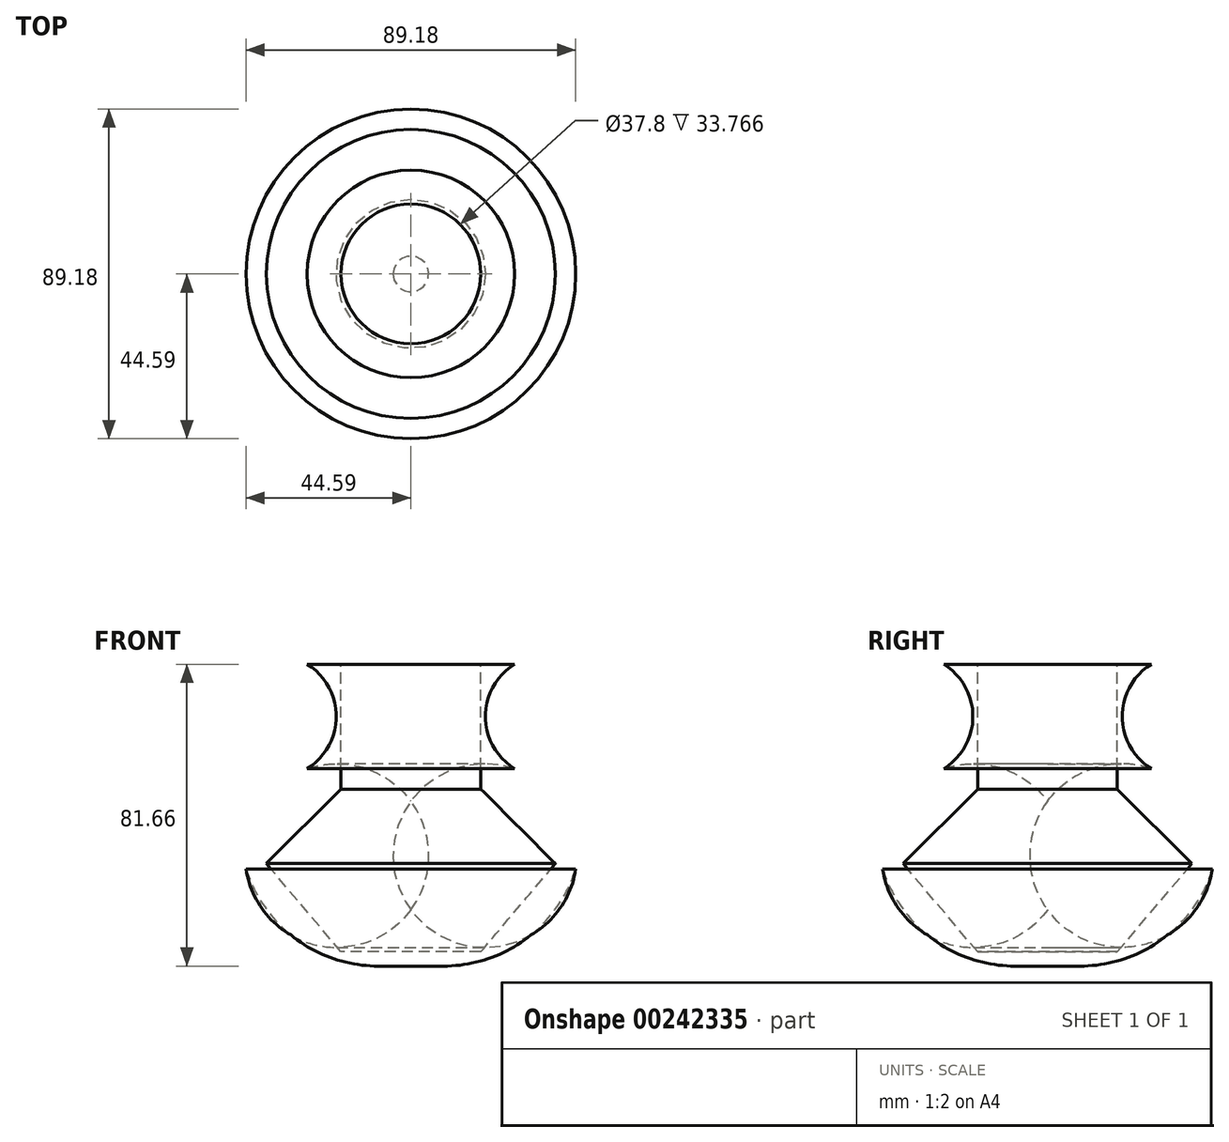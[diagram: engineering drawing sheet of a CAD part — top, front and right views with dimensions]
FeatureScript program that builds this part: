
annotation { "Feature Type Name" : "Feature", "Feature Type Description" : "" }
export const myFeature = defineFeature(function(context is Context, id is Id, definition is map)
    precondition{}
    {
        {
            var Q0;
            Q0=qCreatedBy(makeId("Front.planeOp"),FACE);
            var sketch = newSketch(context, id + "F0", { "sketchPlane" : qUnion([Q0])});
            skLineSegment(sketch, "E0", {"start": v(0, -46.24) * mm, "end": v(-8.8, -46.24) * mm});
            skArc(sketch, "E1", {"start": v(-44.6, -20) * mm, "mid": v(-31, -38.98) * mm, "end": v(-8.8, -46.24) * mm});
            skArc(sketch, "E2", {"start": v(-28.08, 7.16) * mm, "mid": v(-41.25, -3.44) * mm, "end": v(-44.6, -20) * mm});
            skArc(sketch, "E3", {"start": v(-28.08, 7.16) * mm, "mid": v(-20.18, 21.29) * mm, "end": v(-28.08, 35.42) * mm});
            skLineSegment(sketch, "E4", {"start": v(-28.08, 35.42) * mm, "end": v(0, 35.42) * mm});
            skLineSegment(sketch, "E5", {"start": v(0, 35.42) * mm, "end": v(0, -46.24) * mm});
            skSolve(sketch);
        }
        {
            var Q0;
            Q0=makeQuery(id+"F0.imprint","IMPRINT",FACE,{"disambiguationData":[TD([[makeQuery(id+"F0.imprint","IMPRINT",EDGE,{"derivedFrom":sQuery(id+"F0.wireOp",EDGE,"E0")}),-1.0]])]});
            var Q1;
            Q1=sQuery(id+"F0.wireOp",EDGE,"E5");
            revolve(context, id + "F1", {"entities" : qUnion([Q0]), "axis" : qUnion([Q1]), "revolveType" : RevolveType.FULL});
        }
        {
            var Q0;
            Q0=qCreatedBy(makeId("Front.planeOp"),FACE);
            var sketch = newSketch(context, id + "F2", { "sketchPlane" : qUnion([Q0])});
            skLineSegment(sketch, "E6", {"start": v(-18.9, 35.6) * mm, "end": v(-18.9, 1.65) * mm});
            skLineSegment(sketch, "E7", {"start": v(-18.9, 1.65) * mm, "end": v(-39.09, -18.53) * mm});
            skLineSegment(sketch, "E8", {"start": v(-39.09, -18.53) * mm, "end": v(-18.9, -42.4) * mm});
            skLineSegment(sketch, "E9", {"start": v(-18.9, -42.4) * mm, "end": v(0, -42.4) * mm});
            skLineSegment(sketch, "E10", {"start": v(0, -42.4) * mm, "end": v(0, 35.6) * mm});
            skLineSegment(sketch, "E11", {"start": v(0, 35.6) * mm, "end": v(-18.9, 35.6) * mm});
            skSolve(sketch);
        }
        {
            var Q0;
            Q0 = qSketchRegion(id + "F2", true);
            var Q1;
            Q1=sQuery(id+"F2.wireOp",EDGE,"E10");
            revolve(context, id + "F3", {"operationType" : NewBodyOperationType.REMOVE, "entities" : qUnion([Q0]), "axis" : qUnion([Q1]), "revolveType" : RevolveType.FULL, "oppositeDirection" : true});
        }
    });
